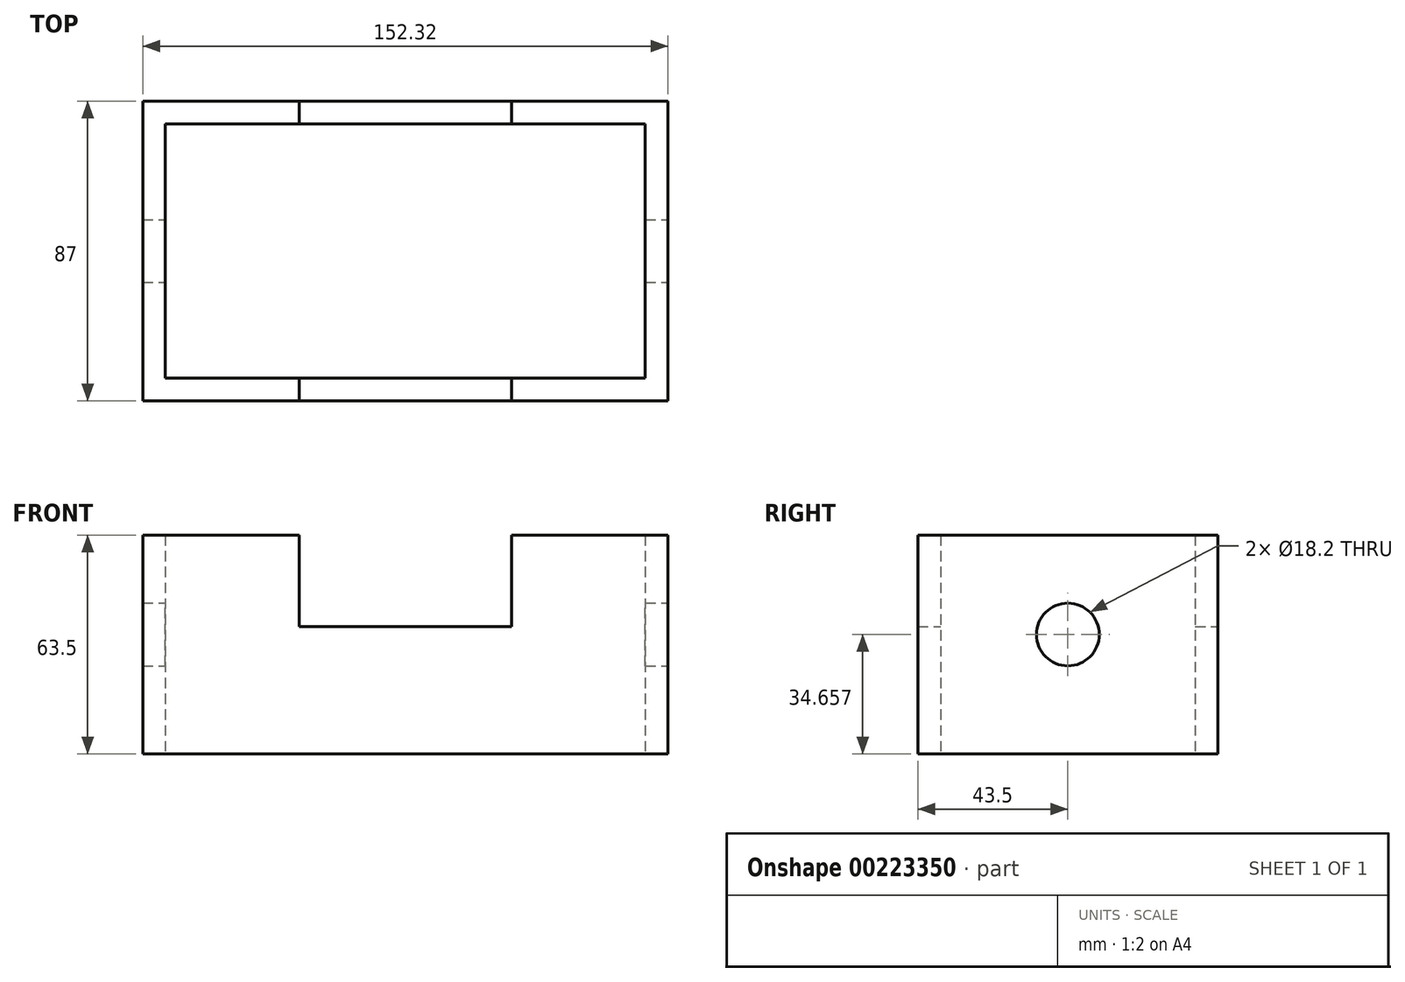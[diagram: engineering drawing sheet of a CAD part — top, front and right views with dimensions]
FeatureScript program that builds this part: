
annotation { "Feature Type Name" : "Feature", "Feature Type Description" : "" }
export const myFeature = defineFeature(function(context is Context, id is Id, definition is map)
    precondition{}
    {
        {
            var Q0;
            Q0=qCreatedBy(makeId("Top.planeOp"),FACE);
            var sketch = newSketch(context, id + "F0", { "sketchPlane" : qUnion([Q0])});
            skLineSegment(sketch, "E0.bottom", {"start": v(-76.16, 43.5) * mm, "end": v(76.16, 43.5) * mm});
            skLineSegment(sketch, "E0.top", {"start": v(-76.16, -43.5) * mm, "end": v(76.16, -43.5) * mm});
            skLineSegment(sketch, "E0.left", {"start": v(-76.16, 43.5) * mm, "end": v(-76.16, -43.5) * mm});
            skLineSegment(sketch, "E0.right", {"start": v(76.16, 43.5) * mm, "end": v(76.16, -43.5) * mm});
            skPoint(sketch, "E0.middle", {"position": v(0, 0) * mm});
            skLineSegment(sketch, "E1.bottom", {"start": v(-69.6, 36.94) * mm, "end": v(69.6, 36.94) * mm});
            skLineSegment(sketch, "E1.top", {"start": v(-69.6, -36.94) * mm, "end": v(69.6, -36.94) * mm});
            skLineSegment(sketch, "E1.left", {"start": v(-69.6, 36.94) * mm, "end": v(-69.6, -36.94) * mm});
            skLineSegment(sketch, "E1.right", {"start": v(69.6, 36.94) * mm, "end": v(69.6, -36.94) * mm});
            skSolve(sketch);
        }
        {
            var Q0;
            Q0 = qSketchRegion(id + "F0", true);
            extrude(context, id + "F1", {"entities" : qUnion([Q0]), "depth" : 63.5 * mm});
        }
        {
            var Q0;
            Q0=qCreatedBy(makeId("Front.planeOp"),FACE);
            var sketch = newSketch(context, id + "F2", { "sketchPlane" : qUnion([Q0])});
            skLineSegment(sketch, "E2.bottom", {"start": v(-30.8, 75.16) * mm, "end": v(30.8, 75.16) * mm});
            skLineSegment(sketch, "E2.top", {"start": v(-30.8, 36.94) * mm, "end": v(30.8, 36.94) * mm});
            skLineSegment(sketch, "E2.left", {"start": v(-30.8, 75.16) * mm, "end": v(-30.8, 36.94) * mm});
            skLineSegment(sketch, "E2.right", {"start": v(30.8, 75.16) * mm, "end": v(30.8, 36.94) * mm});
            skPoint(sketch, "E2.middle", {"position": v(0, 56.05) * mm});
            skSolve(sketch);
        }
        {
            var Q0;
            Q0 = qSketchRegion(id + "F2", true);
            extrude(context, id + "F3", {"entities" : qUnion([Q0]), "operationType" : NewBodyOperationType.REMOVE, "depth" : 50.8 * mm, "hasSecondDirection" : true, "secondDirectionOppositeDirection" : true, "secondDirectionDepth" : 50.8 * mm});
        }
        {
            var Q0;
            Q0=qCreatedBy(makeId("Right.planeOp"),FACE);
            var sketch = newSketch(context, id + "F4", { "sketchPlane" : qUnion([Q0])});
            skCircle(sketch, "E3", {"center": v(0, 34.66) * mm, "radius": 9.1 * mm});
            skSolve(sketch);
        }
        {
            var Q0;
            Q0 = qSketchRegion(id + "F4", true);
            extrude(context, id + "F5", {"entities" : qUnion([Q0]), "operationType" : NewBodyOperationType.REMOVE, "oppositeDirection" : true, "depth" : 101.6 * mm, "hasSecondDirection" : true, "secondDirectionOppositeDirection" : false, "secondDirectionDepth" : 101.6 * mm});
        }
    });
